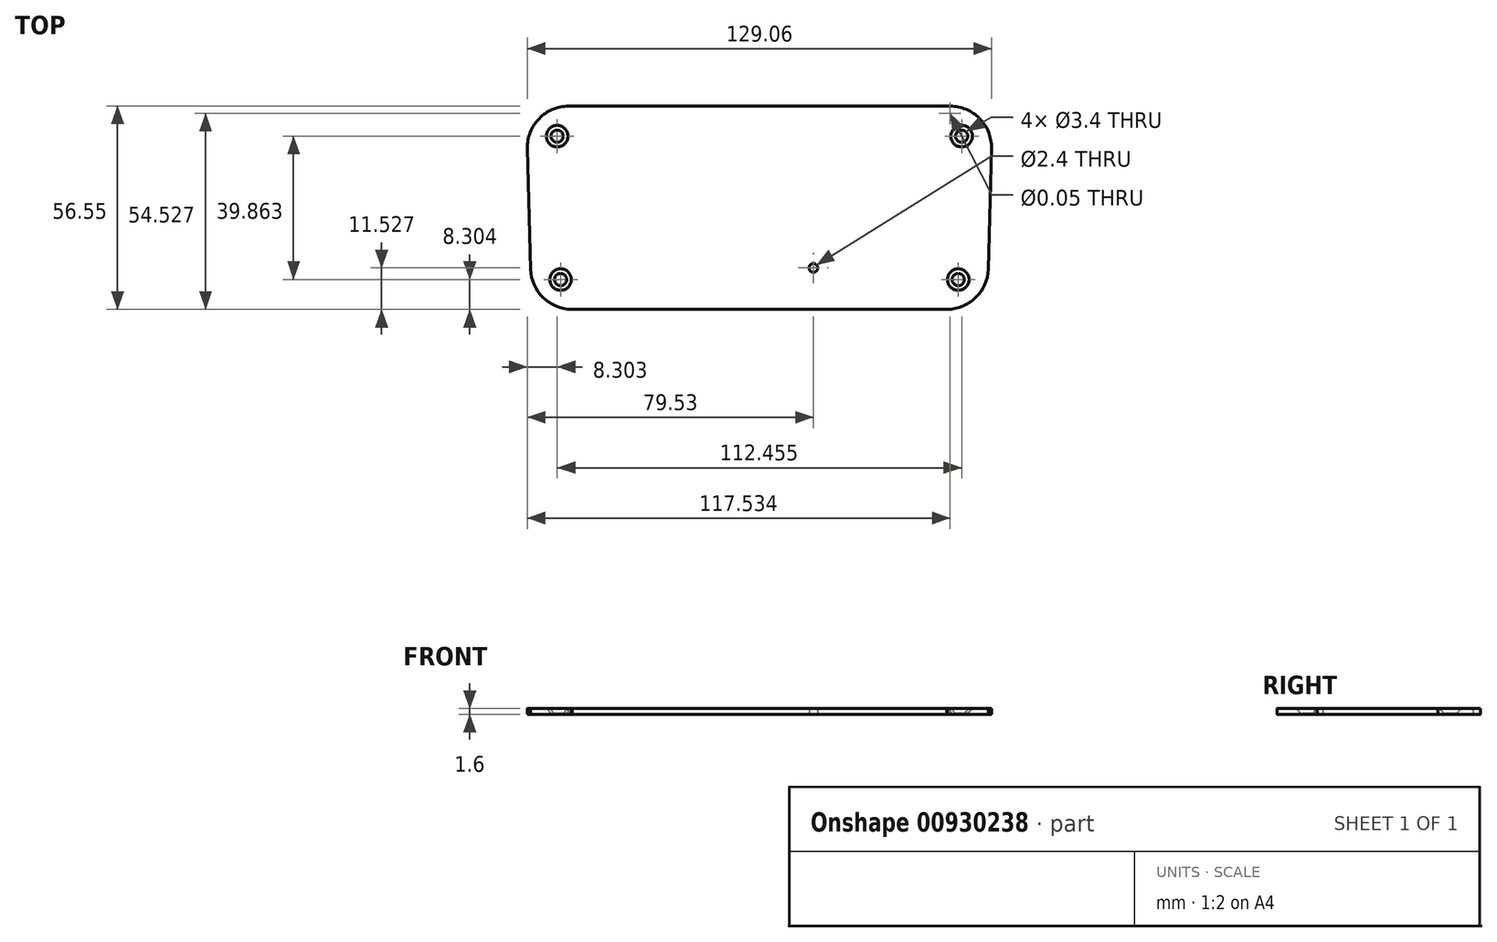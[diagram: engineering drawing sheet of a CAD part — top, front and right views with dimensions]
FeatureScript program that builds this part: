
annotation { "Feature Type Name" : "Feature", "Feature Type Description" : "" }
export const myFeature = defineFeature(function(context is Context, id is Id, definition is map)
    precondition{}
    {
        {
            var Q0;
            Q0=qCreatedBy(makeId("Top.planeOp"),FACE);
            var sketch = newSketch(context, id + "F0", { "sketchPlane" : qUnion([Q0])});
            skArc(sketch, "E0", {"start": v(52.48, 29.69) * mm, "mid": v(52.5, 29.66) * mm, "end": v(52.53, 29.69) * mm});
            skArc(sketch, "E1", {"start": v(52.53, 29.69) * mm, "mid": v(52.5, 29.71) * mm, "end": v(52.48, 29.69) * mm});
            skLineSegment(sketch, "E2", {"start": v(-65, 19.87) * mm, "end": v(-64.12, -13.63) * mm});
            skArc(sketch, "E3", {"start": v(-65.02, 19.87) * mm, "mid": v(-65, 19.85) * mm, "end": v(-64.97, 19.87) * mm});
            skArc(sketch, "E4", {"start": v(-64.97, 19.87) * mm, "mid": v(-65, 19.9) * mm, "end": v(-65.02, 19.87) * mm});
            skArc(sketch, "E5", {"start": v(-64.15, -13.63) * mm, "mid": v(-64.12, -13.65) * mm, "end": v(-64.1, -13.63) * mm});
            skArc(sketch, "E6", {"start": v(-64.1, -13.63) * mm, "mid": v(-64.12, -13.6) * mm, "end": v(-64.15, -13.63) * mm});
            skLineSegment(sketch, "E7", {"start": v(-53.5, 31.69) * mm, "end": v(52.5, 31.69) * mm});
            skArc(sketch, "E8", {"start": v(-53.53, 31.69) * mm, "mid": v(-53.5, 31.66) * mm, "end": v(-53.48, 31.69) * mm});
            skArc(sketch, "E9", {"start": v(-53.48, 31.69) * mm, "mid": v(-53.5, 31.71) * mm, "end": v(-53.53, 31.69) * mm});
            skArc(sketch, "E10", {"start": v(52.48, 31.69) * mm, "mid": v(52.5, 31.66) * mm, "end": v(52.53, 31.69) * mm});
            skArc(sketch, "E11", {"start": v(52.53, 31.69) * mm, "mid": v(52.5, 31.71) * mm, "end": v(52.48, 31.69) * mm});
            skLineSegment(sketch, "E12", {"start": v(63.12, -13.63) * mm, "end": v(64, 19.87) * mm});
            skArc(sketch, "E13", {"start": v(63.1, -13.63) * mm, "mid": v(63.12, -13.65) * mm, "end": v(63.15, -13.63) * mm});
            skArc(sketch, "E14", {"start": v(63.15, -13.63) * mm, "mid": v(63.12, -13.6) * mm, "end": v(63.1, -13.63) * mm});
            skArc(sketch, "E15", {"start": v(63.98, 19.87) * mm, "mid": v(64, 19.85) * mm, "end": v(64.03, 19.87) * mm});
            skArc(sketch, "E16", {"start": v(64.03, 19.87) * mm, "mid": v(64, 19.9) * mm, "end": v(63.98, 19.87) * mm});
            skLineSegment(sketch, "E17", {"start": v(-52.63, -24.81) * mm, "end": v(51.63, -24.81) * mm});
            skArc(sketch, "E18", {"start": v(-52.65, -24.81) * mm, "mid": v(-52.63, -24.84) * mm, "end": v(-52.6, -24.81) * mm});
            skArc(sketch, "E19", {"start": v(-52.6, -24.81) * mm, "mid": v(-52.63, -24.79) * mm, "end": v(-52.65, -24.81) * mm});
            skArc(sketch, "E20", {"start": v(51.6, -24.81) * mm, "mid": v(51.63, -24.84) * mm, "end": v(51.65, -24.81) * mm});
            skArc(sketch, "E21", {"start": v(51.65, -24.81) * mm, "mid": v(51.63, -24.79) * mm, "end": v(51.6, -24.81) * mm});
            skArc(sketch, "E22", {"start": v(-52.63, -24.81) * mm, "mid": v(-60.65, -21.55) * mm, "end": v(-64.12, -13.61) * mm});
            skArc(sketch, "E23", {"start": v(-64.15, -13.61) * mm, "mid": v(-64.12, -13.64) * mm, "end": v(-64.1, -13.61) * mm});
            skArc(sketch, "E24", {"start": v(-64.1, -13.61) * mm, "mid": v(-64.12, -13.59) * mm, "end": v(-64.15, -13.61) * mm});
            skArc(sketch, "E25", {"start": v(-65, 19.89) * mm, "mid": v(-61.74, 28.21) * mm, "end": v(-53.5, 31.69) * mm});
            skArc(sketch, "E26", {"start": v(-65.03, 19.89) * mm, "mid": v(-65, 19.86) * mm, "end": v(-64.98, 19.89) * mm});
            skArc(sketch, "E27", {"start": v(-64.98, 19.89) * mm, "mid": v(-65, 19.91) * mm, "end": v(-65.03, 19.89) * mm});
            skArc(sketch, "E28", {"start": v(52.5, 31.69) * mm, "mid": v(60.74, 28.21) * mm, "end": v(64, 19.89) * mm});
            skArc(sketch, "E29", {"start": v(63.98, 19.89) * mm, "mid": v(64, 19.86) * mm, "end": v(64.03, 19.89) * mm});
            skArc(sketch, "E30", {"start": v(64.03, 19.89) * mm, "mid": v(64, 19.91) * mm, "end": v(63.98, 19.89) * mm});
            skArc(sketch, "E31", {"start": v(63.12, -13.61) * mm, "mid": v(59.65, -21.55) * mm, "end": v(51.63, -24.81) * mm});
            skArc(sketch, "E32", {"start": v(63.1, -13.61) * mm, "mid": v(63.12, -13.64) * mm, "end": v(63.15, -13.61) * mm});
            skArc(sketch, "E33", {"start": v(63.15, -13.61) * mm, "mid": v(63.12, -13.59) * mm, "end": v(63.1, -13.61) * mm});
            skArc(sketch, "E34", {"start": v(54.02, -16.54) * mm, "mid": v(54.77, -17.29) * mm, "end": v(55.52, -16.54) * mm});
            skArc(sketch, "E35", {"start": v(55.52, -16.54) * mm, "mid": v(54.77, -15.79) * mm, "end": v(54.02, -16.54) * mm});
            skArc(sketch, "E36", {"start": v(54.98, 23.33) * mm, "mid": v(55.73, 22.58) * mm, "end": v(56.48, 23.33) * mm});
            skArc(sketch, "E37", {"start": v(56.48, 23.33) * mm, "mid": v(55.73, 24.08) * mm, "end": v(54.98, 23.33) * mm});
            skArc(sketch, "E38", {"start": v(-56.52, -16.54) * mm, "mid": v(-55.77, -17.29) * mm, "end": v(-55.02, -16.54) * mm});
            skArc(sketch, "E39", {"start": v(-55.02, -16.54) * mm, "mid": v(-55.77, -15.79) * mm, "end": v(-56.52, -16.54) * mm});
            skArc(sketch, "E40", {"start": v(-57.48, 23.33) * mm, "mid": v(-56.73, 22.58) * mm, "end": v(-55.98, 23.33) * mm});
            skArc(sketch, "E41", {"start": v(-55.98, 23.33) * mm, "mid": v(-56.73, 24.08) * mm, "end": v(-57.48, 23.33) * mm});
            skArc(sketch, "E42", {"start": v(14.5, -12.14) * mm, "mid": v(13.33, -13.31) * mm, "end": v(14.5, -14.49) * mm});
            skArc(sketch, "E43", {"start": v(14.5, -14.49) * mm, "mid": v(15.67, -13.31) * mm, "end": v(14.5, -12.14) * mm});
            skArc(sketch, "E44", {"start": v(14.5, -12.11) * mm, "mid": v(13.3, -13.31) * mm, "end": v(14.5, -14.51) * mm});
            skArc(sketch, "E45", {"start": v(14.5, -14.51) * mm, "mid": v(15.7, -13.31) * mm, "end": v(14.5, -12.11) * mm});
            skSolve(sketch);
        }
        {
            var Q0;
            Q0 = qSketchRegion(id + "F0", true);
            extrude(context, id + "F1", {"entities" : qUnion([Q0]), "depth" : 1.6 * mm, "offsetDistance" : 25 * mm});
        }
        {
            var Q0;
            Q0=makeQuery(id+"F1.opExtrude","CAP_FACE",FACE,{"disambiguationData":[OSD([sQuery(id+"F0.wireOp",EDGE,"E2"),sQuery(id+"F0.wireOp",EDGE,"E3"),sQuery(id+"F0.wireOp",EDGE,"E4"),sQuery(id+"F0.wireOp",EDGE,"E5"),sQuery(id+"F0.wireOp",EDGE,"E6"),sQuery(id+"F0.wireOp",EDGE,"E7"),sQuery(id+"F0.wireOp",EDGE,"E12"),sQuery(id+"F0.wireOp",EDGE,"E13"),sQuery(id+"F0.wireOp",EDGE,"E14"),sQuery(id+"F0.wireOp",EDGE,"E15"),sQuery(id+"F0.wireOp",EDGE,"E16"),sQuery(id+"F0.wireOp",EDGE,"E17"),sQuery(id+"F0.wireOp",EDGE,"E18"),sQuery(id+"F0.wireOp",EDGE,"E0"),sQuery(id+"F0.wireOp",EDGE,"E1"),sQuery(id+"F0.wireOp",EDGE,"E22"),sQuery(id+"F0.wireOp",EDGE,"E23"),sQuery(id+"F0.wireOp",EDGE,"E24"),sQuery(id+"F0.wireOp",EDGE,"E25"),sQuery(id+"F0.wireOp",EDGE,"E26"),sQuery(id+"F0.wireOp",EDGE,"E27"),sQuery(id+"F0.wireOp",EDGE,"E9"),sQuery(id+"F0.wireOp",EDGE,"E28"),sQuery(id+"F0.wireOp",EDGE,"E11"),sQuery(id+"F0.wireOp",EDGE,"E29"),sQuery(id+"F0.wireOp",EDGE,"E30"),sQuery(id+"F0.wireOp",EDGE,"E31"),sQuery(id+"F0.wireOp",EDGE,"E32"),sQuery(id+"F0.wireOp",EDGE,"E33"),sQuery(id+"F0.wireOp",EDGE,"E20"),sQuery(id+"F0.wireOp",EDGE,"E34"),sQuery(id+"F0.wireOp",EDGE,"E35"),sQuery(id+"F0.wireOp",EDGE,"E36"),sQuery(id+"F0.wireOp",EDGE,"E37"),sQuery(id+"F0.wireOp",EDGE,"E38"),sQuery(id+"F0.wireOp",EDGE,"E39"),sQuery(id+"F0.wireOp",EDGE,"E40"),sQuery(id+"F0.wireOp",EDGE,"E41"),sQuery(id+"F0.wireOp",EDGE,"E44"),sQuery(id+"F0.wireOp",EDGE,"E45")])],"isStart":false});
            var sketch = newSketch(context, id + "F2", { "sketchPlane" : qUnion([Q0])});
            skPoint(sketch, "E46", {"position": v(-56.73, 23.33) * mm});
            skPoint(sketch, "E47", {"position": v(-55.77, -16.54) * mm});
            skPoint(sketch, "E48", {"position": v(55.73, 23.33) * mm});
            skPoint(sketch, "E49", {"position": v(54.77, -16.54) * mm});
            skSolve(sketch);
        }
        {
            var Q0;
            Q0=sQuery(id+"F2.wireOp",VERTEX,"E46");
            var Q1;
            Q1=sQuery(id+"F2.wireOp",VERTEX,"E47");
            var Q2;
            Q2=sQuery(id+"F2.wireOp",VERTEX,"E48");
            var Q3;
            Q3=sQuery(id+"F2.wireOp",VERTEX,"E49");
            var Q4;
            Q4=makeQuery(id+"F1.opExtrude","SWEPT_BODY",BODY,{"disambiguationData":[OSD([sQuery(id+"F0.wireOp",EDGE,"E2"),sQuery(id+"F0.wireOp",EDGE,"E3"),sQuery(id+"F0.wireOp",EDGE,"E4"),sQuery(id+"F0.wireOp",EDGE,"E5"),sQuery(id+"F0.wireOp",EDGE,"E6"),sQuery(id+"F0.wireOp",EDGE,"E7"),sQuery(id+"F0.wireOp",EDGE,"E12"),sQuery(id+"F0.wireOp",EDGE,"E13"),sQuery(id+"F0.wireOp",EDGE,"E14"),sQuery(id+"F0.wireOp",EDGE,"E15"),sQuery(id+"F0.wireOp",EDGE,"E16"),sQuery(id+"F0.wireOp",EDGE,"E17"),sQuery(id+"F0.wireOp",EDGE,"E18"),sQuery(id+"F0.wireOp",EDGE,"E0"),sQuery(id+"F0.wireOp",EDGE,"E1"),sQuery(id+"F0.wireOp",EDGE,"E22"),sQuery(id+"F0.wireOp",EDGE,"E23"),sQuery(id+"F0.wireOp",EDGE,"E24"),sQuery(id+"F0.wireOp",EDGE,"E25"),sQuery(id+"F0.wireOp",EDGE,"E26"),sQuery(id+"F0.wireOp",EDGE,"E27"),sQuery(id+"F0.wireOp",EDGE,"E9"),sQuery(id+"F0.wireOp",EDGE,"E28"),sQuery(id+"F0.wireOp",EDGE,"E11"),sQuery(id+"F0.wireOp",EDGE,"E29"),sQuery(id+"F0.wireOp",EDGE,"E30"),sQuery(id+"F0.wireOp",EDGE,"E31"),sQuery(id+"F0.wireOp",EDGE,"E32"),sQuery(id+"F0.wireOp",EDGE,"E33"),sQuery(id+"F0.wireOp",EDGE,"E20"),sQuery(id+"F0.wireOp",EDGE,"E34"),sQuery(id+"F0.wireOp",EDGE,"E35"),sQuery(id+"F0.wireOp",EDGE,"E36"),sQuery(id+"F0.wireOp",EDGE,"E37"),sQuery(id+"F0.wireOp",EDGE,"E38"),sQuery(id+"F0.wireOp",EDGE,"E39"),sQuery(id+"F0.wireOp",EDGE,"E40"),sQuery(id+"F0.wireOp",EDGE,"E41"),sQuery(id+"F0.wireOp",EDGE,"E44"),sQuery(id+"F0.wireOp",EDGE,"E45")])]});
            hole(context, id + "F3", {"style" : HoleStyle.C_SINK, "endStyle" : HoleEndStyle.THROUGH, "holeDiameter" : 3.4 * mm, "cSinkDiameter" : 6 * mm, "cSinkAngle" : 90 * degree, "majorDiameter" : 5 * mm, "isTappedThrough" : true, "tappedDepth" : 12 * mm, "tapClearance" : 3, "startFromSketch" : true, "locations" : qUnion([Q0, Q1, Q2, Q3]), "scope" : qUnion([Q4])});
        }
    });
